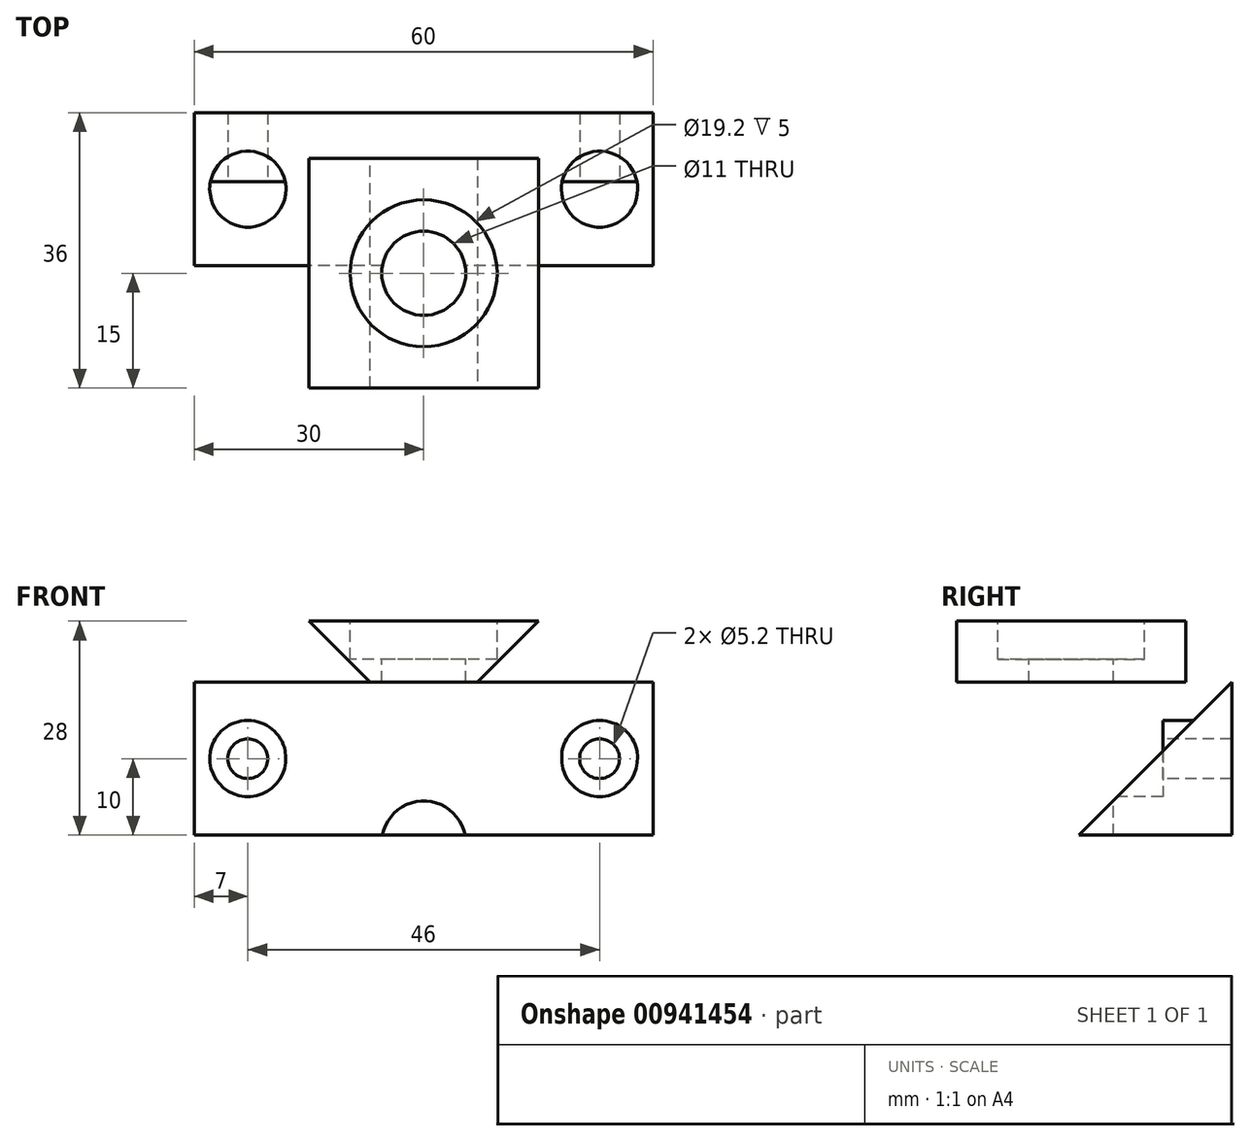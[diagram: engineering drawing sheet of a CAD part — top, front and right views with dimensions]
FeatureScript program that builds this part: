
annotation { "Feature Type Name" : "Feature", "Feature Type Description" : "" }
export const myFeature = defineFeature(function(context is Context, id is Id, definition is map)
    precondition{}
    {
        {
            var Q0;
            Q0=qCreatedBy(makeId("Front.planeOp"),FACE);
            var sketch = newSketch(context, id + "F0", { "sketchPlane" : qUnion([Q0])});
            skLineSegment(sketch, "E0.bottom", {"start": v(30, -10) * mm, "end": v(-30, -10) * mm});
            skLineSegment(sketch, "E0.top", {"start": v(30, 10) * mm, "end": v(-30, 10) * mm});
            skLineSegment(sketch, "E0.left", {"start": v(30, -10) * mm, "end": v(30, 10) * mm});
            skLineSegment(sketch, "E0.right", {"start": v(-30, -10) * mm, "end": v(-30, 10) * mm});
            skPoint(sketch, "E0.middle", {"position": v(0, 0) * mm});
            skSolve(sketch);
        }
        {
            var Q0;
            Q0=makeQuery(id+"F0.imprint","IMPRINT",FACE,{"disambiguationData":[TD([[makeQuery(id+"F0.imprint","IMPRINT",EDGE,{"derivedFrom":sQuery(id+"F0.wireOp",EDGE,"E0.bottom")}),-1.0]])]});
            extrude(context, id + "F1", {"entities" : qUnion([Q0]), "depth" : 20 * mm, "offsetDistance" : 25 * mm});
        }
        {
            var Q0;
            Q0=makeQuery(id+"F1.opExtrude","SWEPT_FACE",FACE,{"disambiguationData":[OSD([sQuery(id+"F0.wireOp",EDGE,"E0.top")])]});
            var sketch = newSketch(context, id + "F2", { "sketchPlane" : qUnion([Q0])});
            skLineSegment(sketch, "E1.bottom", {"start": v(15, -36) * mm, "end": v(-15, -36) * mm});
            skLineSegment(sketch, "E1.top", {"start": v(15, -6) * mm, "end": v(-15, -6) * mm});
            skLineSegment(sketch, "E1.left", {"start": v(15, -36) * mm, "end": v(15, -6) * mm});
            skLineSegment(sketch, "E1.right", {"start": v(-15, -36) * mm, "end": v(-15, -6) * mm});
            skPoint(sketch, "E1.middle", {"position": v(0, -21) * mm});
            skPoint(sketch, "E2.oppositeSnap0", {"position": v(0, 0) * mm});
            skLineSegment(sketch, "E2.bottom", {"start": v(-15, -6) * mm, "end": v(15, -6) * mm});
            skLineSegment(sketch, "E2.top", {"start": v(-15, 0) * mm, "end": v(15, 0) * mm});
            skLineSegment(sketch, "E2.left", {"start": v(-15, -6) * mm, "end": v(-15, 0) * mm});
            skLineSegment(sketch, "E2.right", {"start": v(15, -6) * mm, "end": v(15, 0) * mm});
            skSolve(sketch);
        }
        {
            var Q0;
            {var subQ0=sQuery(id+"F2.wireOp",EDGE,"E1.top");Q0=makeQuery(id+"F2.imprint","IMPRINT",FACE,{"disambiguationData":[TD([[makeQuery(id+"F2.imprint","IMPRINT",EDGE,{"derivedFrom":subQ0}),1.0]])]});}
            var Q1;
            {var subQ0=sQuery(id+"F2.wireOp",EDGE,"E1.bottom");Q1=makeQuery(id+"F2.imprint","IMPRINT",FACE,{"disambiguationData":[TD([[makeQuery(id+"F2.imprint","IMPRINT",EDGE,{"derivedFrom":subQ0}),-1.0]])]});}
            var Q2;
            {var subQ0=sQuery(id+"F2.wireOp",EDGE,"E2.bottom");Q2=makeQuery(id+"F2.imprint","IMPRINT",FACE,{"disambiguationData":[TD([[makeQuery(id+"F2.imprint","IMPRINT",EDGE,{"derivedFrom":subQ0}),-1.0]])]});}
            var Q3;
            Q3=makeQuery(id+"F2.imprint","IMPRINT",FACE,{"disambiguationData":[TD([[makeQuery(id+"F2.imprint","IMPRINT",EDGE,{"derivedFrom":sQuery(id+"F2.wireOp",EDGE,"E2.bottom")}),1.0]])]});
            extrude(context, id + "F3", {"entities" : qUnion([Q0, Q1, Q2, Q3]), "operationType" : NewBodyOperationType.ADD, "depth" : 8 * mm, "offsetDistance" : 25 * mm});
        }
        {
            var Q0;
            Q0=makeQuery(id+"F3.opExtrude","CAP_FACE",FACE,{"disambiguationData":[OSD([sQuery(id+"F2.wireOp",EDGE,"E1.bottom"),sQuery(id+"F2.wireOp",EDGE,"E1.top"),sQuery(id+"F2.wireOp",EDGE,"E1.left"),sQuery(id+"F2.wireOp",EDGE,"E1.right")])],"isStart":false});
            var sketch = newSketch(context, id + "F4", { "sketchPlane" : qUnion([Q0])});
            skCircle(sketch, "E3", {"center": v(0, -21) * mm, "radius": 9.6 * mm});
            skSolve(sketch);
        }
        {
            var Q0;
            Q0=makeQuery(id+"F4.imprint","IMPRINT",FACE,{"disambiguationData":[TD([[makeQuery(id+"F4.imprint","IMPRINT",EDGE,{"derivedFrom":sQuery(id+"F4.wireOp",EDGE,"E3")}),1.0]])]});
            extrude(context, id + "F5", {"entities" : qUnion([Q0]), "operationType" : NewBodyOperationType.REMOVE, "oppositeDirection" : true, "depth" : 5 * mm, "offsetDistance" : 25 * mm});
        }
        {
            var Q0;
            Q0=makeQuery(id+"F1.opExtrude","CAP_FACE",FACE,{"disambiguationData":[OSD([sQuery(id+"F0.wireOp",EDGE,"E0.bottom"),sQuery(id+"F0.wireOp",EDGE,"E0.top"),sQuery(id+"F0.wireOp",EDGE,"E0.left"),sQuery(id+"F0.wireOp",EDGE,"E0.right")])],"isStart":false});
            var sketch = newSketch(context, id + "F6", { "sketchPlane" : qUnion([Q0])});
            skCircle(sketch, "E4", {"center": v(-23, 0) * mm, "radius": 2.6 * mm});
            skPoint(sketch, "E4.centerSnap0", {"position": v(-30, 0) * mm});
            skCircle(sketch, "E5", {"center": v(23, 0) * mm, "radius": 2.6 * mm});
            skSolve(sketch);
        }
        {
            var Q0;
            Q0=makeQuery(id+"F6.imprint","IMPRINT",FACE,{"disambiguationData":[TD([[makeQuery(id+"F6.imprint","IMPRINT",EDGE,{"derivedFrom":sQuery(id+"F6.wireOp",EDGE,"E4")}),1.0]])]});
            var Q1;
            Q1=makeQuery(id+"F6.imprint","IMPRINT",FACE,{"disambiguationData":[TD([[makeQuery(id+"F6.imprint","IMPRINT",EDGE,{"derivedFrom":sQuery(id+"F6.wireOp",EDGE,"E5")}),1.0]])]});
            extrude(context, id + "F7", {"entities" : qUnion([Q0, Q1]), "operationType" : NewBodyOperationType.REMOVE, "oppositeDirection" : true, "depth" : 25 * mm, "offsetDistance" : 25 * mm});
        }
        {
            var Q0;
            Q0=makeQuery(id+"F1.opExtrude","CAP_FACE",FACE,{"disambiguationData":[OSD([sQuery(id+"F0.wireOp",EDGE,"E0.bottom"),sQuery(id+"F0.wireOp",EDGE,"E0.top"),sQuery(id+"F0.wireOp",EDGE,"E0.left"),sQuery(id+"F0.wireOp",EDGE,"E0.right")])],"isStart":false});
            var sketch = newSketch(context, id + "F8", { "sketchPlane" : qUnion([Q0])});
            skCircle(sketch, "E6", {"center": v(-23, 0) * mm, "radius": 5 * mm});
            skCircle(sketch, "E7", {"center": v(23, 0) * mm, "radius": 5 * mm});
            skSolve(sketch);
        }
        {
            var Q0;
            Q0=makeQuery(id+"F8.imprint","IMPRINT",FACE,{"disambiguationData":[TD([[makeQuery(id+"F8.imprint","IMPRINT",EDGE,{"derivedFrom":sQuery(id+"F8.wireOp",EDGE,"E6")}),1.0]])]});
            var Q1;
            Q1=makeQuery(id+"F8.imprint","IMPRINT",FACE,{"disambiguationData":[TD([[makeQuery(id+"F8.imprint","IMPRINT",EDGE,{"derivedFrom":sQuery(id+"F8.wireOp",EDGE,"E7")}),1.0]])]});
            extrude(context, id + "F9", {"entities" : qUnion([Q0, Q1]), "operationType" : NewBodyOperationType.REMOVE, "oppositeDirection" : true, "depth" : 11 * mm, "offsetDistance" : 25 * mm});
        }
        {
            var Q0;
            {var subQ0=sQuery(id+"F0.wireOp",EDGE,"E0.top");Q0=makeQuery(id+"F3.boolean.opBoolean","SPLIT",EDGE,{"disambiguationData":[topologyDisambiguationEdgeConnected([makeQuery(id+"F1.opExtrude","CAP_FACE",FACE,{"disambiguationData":[OSD([sQuery(id+"F0.wireOp",EDGE,"E0.bottom"),subQ0,sQuery(id+"F0.wireOp",EDGE,"E0.left"),sQuery(id+"F0.wireOp",EDGE,"E0.right")])],"isStart":false}),makeQuery(id+"F3.opExtrude","CAP_FACE",FACE,{"disambiguationData":[OSD([sQuery(id+"F2.wireOp",EDGE,"E1.bottom"),sQuery(id+"F2.wireOp",EDGE,"E1.left"),sQuery(id+"F2.wireOp",EDGE,"E1.right"),sQuery(id+"F2.wireOp",EDGE,"E2.top"),sQuery(id+"F2.wireOp",EDGE,"E2.left"),sQuery(id+"F2.wireOp",EDGE,"E2.right")])],"isStart":true})])],"derivedFrom":makeQuery(id+"F1.opExtrude","CAP_EDGE",EDGE,{"disambiguationData":[OSD([subQ0])],"isStart":false})});}
            chamfer(context, id + "F10", {"entities" : qUnion([Q0]), "width" : 20 * mm, "tangentPropagation" : true});
        }
        {
            var Q0;
            Q0=makeQuery(id+"F5.boolean.opBoolean","COPY",FACE,{"derivedFrom":makeQuery(id+"F5.opExtrude","CAP_FACE",FACE,{"disambiguationData":[OSD([sQuery(id+"F4.wireOp",EDGE,"E3")])],"isStart":false})});
            var sketch = newSketch(context, id + "F11", { "sketchPlane" : qUnion([Q0])});
            skCircle(sketch, "E8", {"center": v(0, -21) * mm, "radius": 5.5 * mm});
            skSolve(sketch);
        }
        {
            var Q0;
            Q0=makeQuery(id+"F11.imprint","IMPRINT",FACE,{"disambiguationData":[TD([[makeQuery(id+"F11.imprint","IMPRINT",EDGE,{"derivedFrom":sQuery(id+"F11.wireOp",EDGE,"E8")}),1.0]])]});
            extrude(context, id + "F12", {"entities" : qUnion([Q0]), "operationType" : NewBodyOperationType.REMOVE, "oppositeDirection" : true, "depth" : 25 * mm, "offsetDistance" : 25 * mm});
        }
        {
            var Q0;
            {var subQ0=sQuery(id+"F2.wireOp",EDGE,"E2.left");var subQ1=sQuery(id+"F2.wireOp",EDGE,"E1.right");Q0=makeQuery(id+"F3.boolean.opBoolean","SPLIT",EDGE,{"disambiguationData":[topologyDisambiguationEdgeConnected([makeQuery(id+"F1.opExtrude","SWEPT_FACE",FACE,{"disambiguationData":[OSD([sQuery(id+"F0.wireOp",EDGE,"E0.top")])]})])],"derivedFrom":makeQuery(id+"F3.opExtrude","CAP_EDGE",EDGE,{"disambiguationData":[OSD([subQ1,subQ0])],"isStart":true})});}
            var Q1;
            {var subQ0=sQuery(id+"F2.wireOp",EDGE,"E2.right");var subQ1=sQuery(id+"F2.wireOp",EDGE,"E1.left");Q1=makeQuery(id+"F3.boolean.opBoolean","SPLIT",EDGE,{"disambiguationData":[topologyDisambiguationEdgeConnected([makeQuery(id+"F1.opExtrude","SWEPT_FACE",FACE,{"disambiguationData":[OSD([sQuery(id+"F0.wireOp",EDGE,"E0.top")])]})])],"derivedFrom":makeQuery(id+"F3.opExtrude","CAP_EDGE",EDGE,{"disambiguationData":[OSD([subQ1,subQ0])],"isStart":true})});}
            chamfer(context, id + "F13", {"entities" : qUnion([Q0, Q1]), "width" : 8 * mm, "tangentPropagation" : true});
        }
    });
